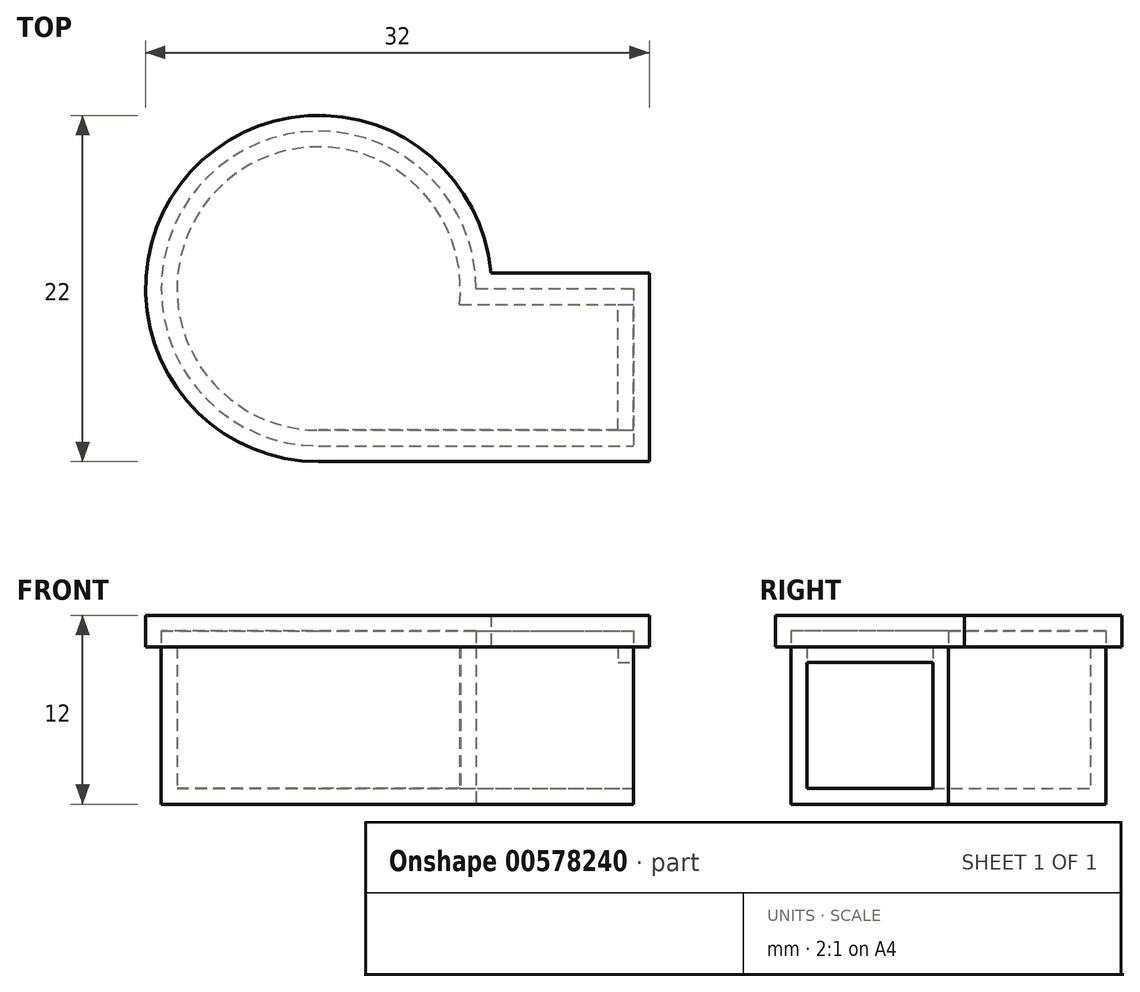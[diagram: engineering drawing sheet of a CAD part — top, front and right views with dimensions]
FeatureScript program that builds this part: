
annotation { "Feature Type Name" : "Feature", "Feature Type Description" : "" }
export const myFeature = defineFeature(function(context is Context, id is Id, definition is map)
    precondition{}
    {
        {
            var Q0;
            Q0=qCreatedBy(makeId("Top.planeOp"),FACE);
            var sketch = newSketch(context, id + "F0", { "sketchPlane" : qUnion([Q0])});
            skCircle(sketch, "E0", {"center": v(0, 0) * mm, "radius": 10 * mm});
            skLineSegment(sketch, "E1.bottom", {"start": v(0, 0) * mm, "end": v(20, 0) * mm});
            skLineSegment(sketch, "E1.top", {"start": v(0, -10) * mm, "end": v(20, -10) * mm});
            skLineSegment(sketch, "E1.left", {"start": v(0, 0) * mm, "end": v(0, -10) * mm});
            skLineSegment(sketch, "E1.right", {"start": v(20, 0) * mm, "end": v(20, -10) * mm});
            skSolve(sketch);
        }
        {
            var Q0;
            {var subQ0=sQuery(id+"F0.wireOp",EDGE,"E1.left");Q0=makeQuery(id+"F0.imprint","IMPRINT",FACE,{"disambiguationData":[TD([[makeQuery(id+"F0.imprint","IMPRINT",EDGE,{"derivedFrom":subQ0}),1.0]])]});}
            var Q1;
            {var subQ0=sQuery(id+"F0.wireOp",EDGE,"E1.top");Q1=makeQuery(id+"F0.imprint","IMPRINT",FACE,{"disambiguationData":[TD([[makeQuery(id+"F0.imprint","IMPRINT",EDGE,{"derivedFrom":subQ0}),1.0]])]});}
            var Q2;
            {var subQ0=sQuery(id+"F0.wireOp",EDGE,"E1.left");Q2=makeQuery(id+"F0.imprint","IMPRINT",FACE,{"disambiguationData":[TD([[makeQuery(id+"F0.imprint","IMPRINT",EDGE,{"derivedFrom":subQ0}),-1.0]])]});}
            extrude(context, id + "F1", {"entities" : qUnion([Q0, Q1, Q2]), "depth" : 10 * mm, "offsetDistance" : 25 * mm});
        }
        {
            var Q0;
            Q0=makeQuery(id+"F1.opExtrude","CAP_FACE",FACE,{"disambiguationData":[OSD([sQuery(id+"F0.wireOp",EDGE,"E0"),sQuery(id+"F0.wireOp",EDGE,"E1.bottom"),sQuery(id+"F0.wireOp",EDGE,"E1.top"),sQuery(id+"F0.wireOp",EDGE,"E1.right")])],"isStart":true});
            var sketch = newSketch(context, id + "F2", { "sketchPlane" : qUnion([Q0])});
            skArc(sketch, "E2.0", {"start": v(0, 9) * mm, "mid": v(-6, -6.7) * mm, "end": v(8.94, 1) * mm});
            skLineSegment(sketch, "E2.1", {"start": v(19, 9) * mm, "end": v(0, 9) * mm});
            skLineSegment(sketch, "E2.2", {"start": v(19, 1) * mm, "end": v(19, 9) * mm});
            skLineSegment(sketch, "E2.3", {"start": v(8.94, 1) * mm, "end": v(19, 1) * mm});
            skSolve(sketch);
        }
        {
            var Q0;
            Q0=makeQuery(id+"F2.imprint","IMPRINT",FACE,{"disambiguationData":[TD([[makeQuery(id+"F2.imprint","IMPRINT",EDGE,{"derivedFrom":sQuery(id+"F2.wireOp",EDGE,"E2.0")}),1.0]])]});
            extrude(context, id + "F3", {"entities" : qUnion([Q0]), "operationType" : NewBodyOperationType.REMOVE, "endBound" : BoundingType.UP_TO_NEXT, "oppositeDirection" : true, "depth" : 25 * mm, "offsetDistance" : 25 * mm});
        }
        {
            var Q0;
            Q0=makeQuery(id+"F1.opExtrude","SWEPT_FACE",FACE,{"disambiguationData":[OSD([sQuery(id+"F0.wireOp",EDGE,"E1.right")])]});
            var sketch = newSketch(context, id + "F4", { "sketchPlane" : qUnion([Q0])});
            skLineSegment(sketch, "E3.0", {"start": v(-9, 1) * mm, "end": v(-1, 1) * mm});
            skLineSegment(sketch, "E3.1", {"start": v(-9, 9) * mm, "end": v(-9, 1) * mm});
            skLineSegment(sketch, "E3.2", {"start": v(-1, 9) * mm, "end": v(-9, 9) * mm});
            skLineSegment(sketch, "E3.3", {"start": v(-1, 1) * mm, "end": v(-1, 9) * mm});
            skSolve(sketch);
        }
        {
            var Q0;
            Q0=makeQuery(id+"F4.imprint","IMPRINT",FACE,{"disambiguationData":[TD([[makeQuery(id+"F4.imprint","IMPRINT",EDGE,{"derivedFrom":sQuery(id+"F4.wireOp",EDGE,"E3.0")}),1.0]])]});
            extrude(context, id + "F5", {"entities" : qUnion([Q0]), "operationType" : NewBodyOperationType.REMOVE, "endBound" : BoundingType.UP_TO_NEXT, "oppositeDirection" : true, "depth" : 25 * mm, "offsetDistance" : 25 * mm});
        }
        {
            var Q0;
            Q0=qCreatedBy(makeId("Top.planeOp"),FACE);
            var sketch = newSketch(context, id + "F6", { "sketchPlane" : qUnion([Q0])});
            skLineSegment(sketch, "E4.0", {"start": v(10, 0) * mm, "end": v(20, 0) * mm});
            skArc(sketch, "E4.1", {"start": v(10, 0) * mm, "mid": v(-7.07, 7.07) * mm, "end": v(0, -10) * mm});
            skLineSegment(sketch, "E4.2", {"start": v(0, -10) * mm, "end": v(20, -10) * mm});
            skLineSegment(sketch, "E4.3", {"start": v(20, 0) * mm, "end": v(20, -10) * mm});
            skSolve(sketch);
        }
        {
            var Q0;
            Q0 = qSketchRegion(id + "F6", true);
            extrude(context, id + "F7", {"entities" : qUnion([Q0]), "operationType" : NewBodyOperationType.ADD, "depth" : 1 * mm, "offsetDistance" : 25 * mm});
        }
        {
            var Q0;
            Q0=makeQuery(id+"F1.opExtrude","CAP_FACE",FACE,{"disambiguationData":[OSD([sQuery(id+"F0.wireOp",EDGE,"E0"),sQuery(id+"F0.wireOp",EDGE,"E1.bottom"),sQuery(id+"F0.wireOp",EDGE,"E1.top"),sQuery(id+"F0.wireOp",EDGE,"E1.right")])],"isStart":false});
            var sketch = newSketch(context, id + "F8", { "sketchPlane" : qUnion([Q0])});
            skLineSegment(sketch, "E5.0", {"start": v(10.95, 1) * mm, "end": v(21, 1) * mm});
            skArc(sketch, "E5.1", {"start": v(10.95, 1) * mm, "mid": v(-8.12, 7.42) * mm, "end": v(0, -11) * mm});
            skLineSegment(sketch, "E5.2", {"start": v(0, -11) * mm, "end": v(21, -11) * mm});
            skLineSegment(sketch, "E5.3", {"start": v(21, 1) * mm, "end": v(21, -11) * mm});
            skSolve(sketch);
        }
        {
            var Q0;
            Q0=makeQuery(id+"F8.imprint","IMPRINT",FACE,{"disambiguationData":[TD([[makeQuery(id+"F8.imprint","IMPRINT",EDGE,{"derivedFrom":sQuery(id+"F8.wireOp",EDGE,"E5.0")}),-1.0]])]});
            extrude(context, id + "F9", {"entities" : qUnion([Q0]), "depth" : 2 * mm, "offsetDistance" : 25 * mm});
        }
        {
            var Q0;
            Q0=makeQuery(id+"F9.opExtrude","CAP_FACE",FACE,{"disambiguationData":[OSD([sQuery(id+"F0.wireOp",EDGE,"E0"),sQuery(id+"F0.wireOp",EDGE,"E1.bottom"),sQuery(id+"F0.wireOp",EDGE,"E1.top"),sQuery(id+"F0.wireOp",EDGE,"E1.right"),sQuery(id+"F8.wireOp",EDGE,"E5.0"),sQuery(id+"F8.wireOp",EDGE,"E5.1"),sQuery(id+"F8.wireOp",EDGE,"E5.2"),sQuery(id+"F8.wireOp",EDGE,"E5.3")])],"isStart":false});
            var sketch = newSketch(context, id + "F10", { "sketchPlane" : qUnion([Q0])});
            skArc(sketch, "E6.0", {"start": v(10, 0) * mm, "mid": v(-7.07, 7.07) * mm, "end": v(0, -10) * mm});
            skLineSegment(sketch, "E6.1", {"start": v(10, 0) * mm, "end": v(20, 0) * mm});
            skLineSegment(sketch, "E6.2", {"start": v(20, 0) * mm, "end": v(20, -10) * mm});
            skLineSegment(sketch, "E6.3", {"start": v(0, -10) * mm, "end": v(20, -10) * mm});
            skSolve(sketch);
        }
        {
            var Q0;
            Q0=makeQuery(id+"F10.imprint","IMPRINT",FACE,{"disambiguationData":[TD([[makeQuery(id+"F10.imprint","IMPRINT",EDGE,{"derivedFrom":sQuery(id+"F10.wireOp",EDGE,"E6.0")}),1.0]])]});
            extrude(context, id + "F11", {"entities" : qUnion([Q0]), "operationType" : NewBodyOperationType.ADD, "oppositeDirection" : true, "depth" : 1 * mm, "offsetDistance" : 25 * mm});
        }
    });
